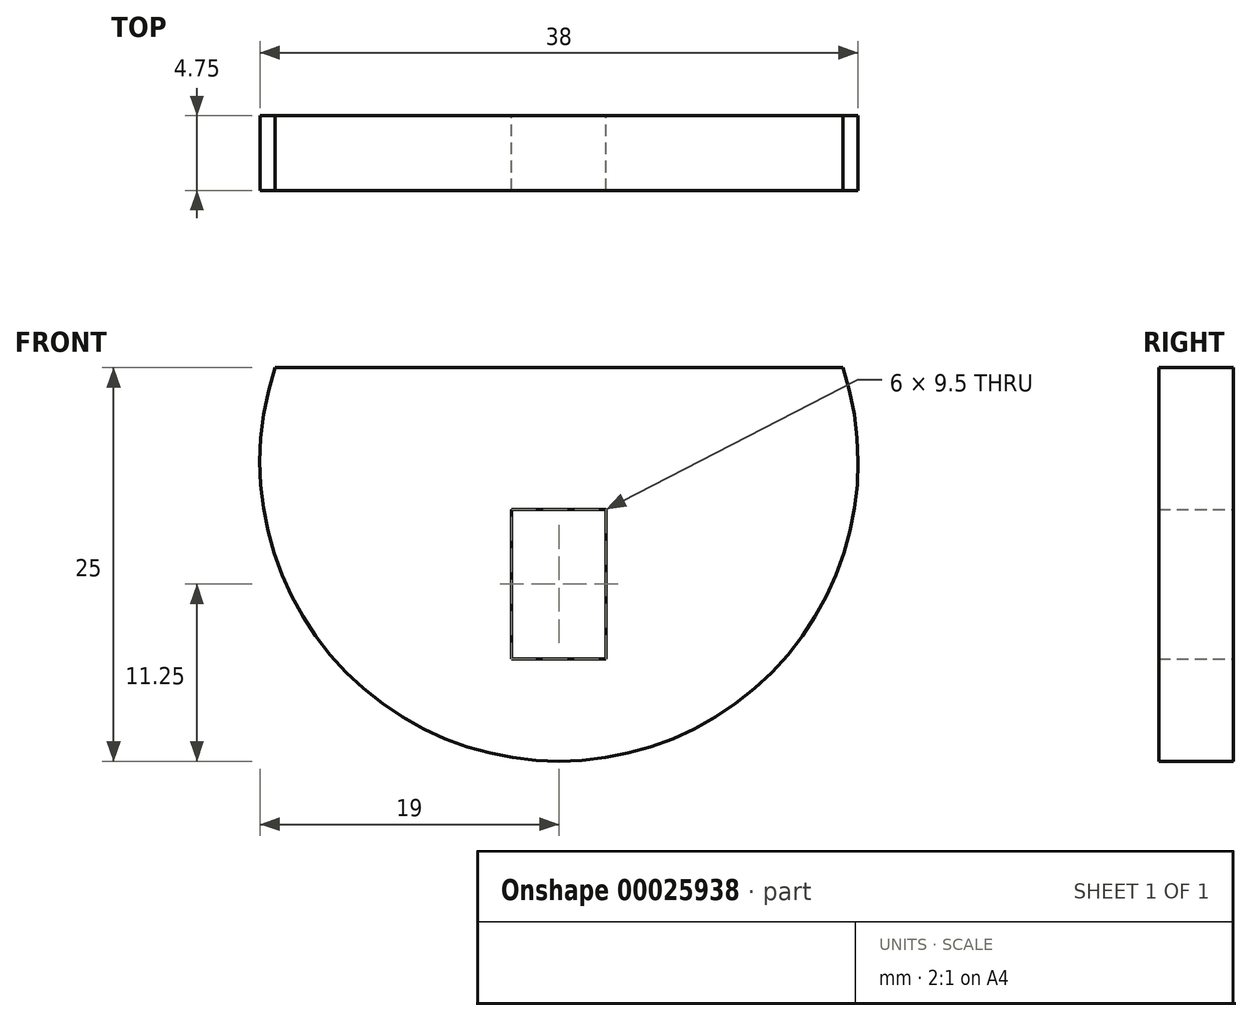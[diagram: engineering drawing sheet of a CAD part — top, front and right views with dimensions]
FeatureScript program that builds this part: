
annotation { "Feature Type Name" : "Feature", "Feature Type Description" : "" }
export const myFeature = defineFeature(function(context is Context, id is Id, definition is map)
    precondition{}
    {
        {
            var Q0;
            Q0=qCreatedBy(makeId("Front.planeOp"),FACE);
            var sketch = newSketch(context, id + "F0", { "sketchPlane" : qUnion([Q0])});
            skArc(sketch, "E0", {"start": v(-18.03, 6) * mm, "mid": v(0, -19) * mm, "end": v(18.03, 6) * mm});
            skLineSegment(sketch, "E1", {"start": v(0, -3) * mm, "end": v(-3, -3) * mm});
            skLineSegment(sketch, "E2", {"start": v(-3, -3) * mm, "end": v(-3, -12.5) * mm});
            skLineSegment(sketch, "E3", {"start": v(-3, -12.5) * mm, "end": v(0, -12.5) * mm});
            skLineSegment(sketch, "E4.MirrorCS", {"start": v(0, -3) * mm, "end": v(3, -3) * mm});
            skLineSegment(sketch, "E5.MirrorCS", {"start": v(3, -3) * mm, "end": v(3, -12.5) * mm});
            skLineSegment(sketch, "E6.MirrorCS", {"start": v(3, -12.5) * mm, "end": v(0, -12.5) * mm});
            skLineSegment(sketch, "E7", {"start": v(-18.03, 6) * mm, "end": v(18.03, 6) * mm});
            skSolve(sketch);
        }
        {
            var Q0;
            Q0=makeQuery(id+"F0.imprint","IMPRINT",FACE,{"disambiguationData":[TD([[makeQuery(id+"F0.imprint","IMPRINT",EDGE,{"derivedFrom":sQuery(id+"F0.wireOp",EDGE,"E0")}),1.0]])]});
            extrude(context, id + "F1", {"entities" : qUnion([Q0]), "depth" : 4.75 * mm});
        }
    });
